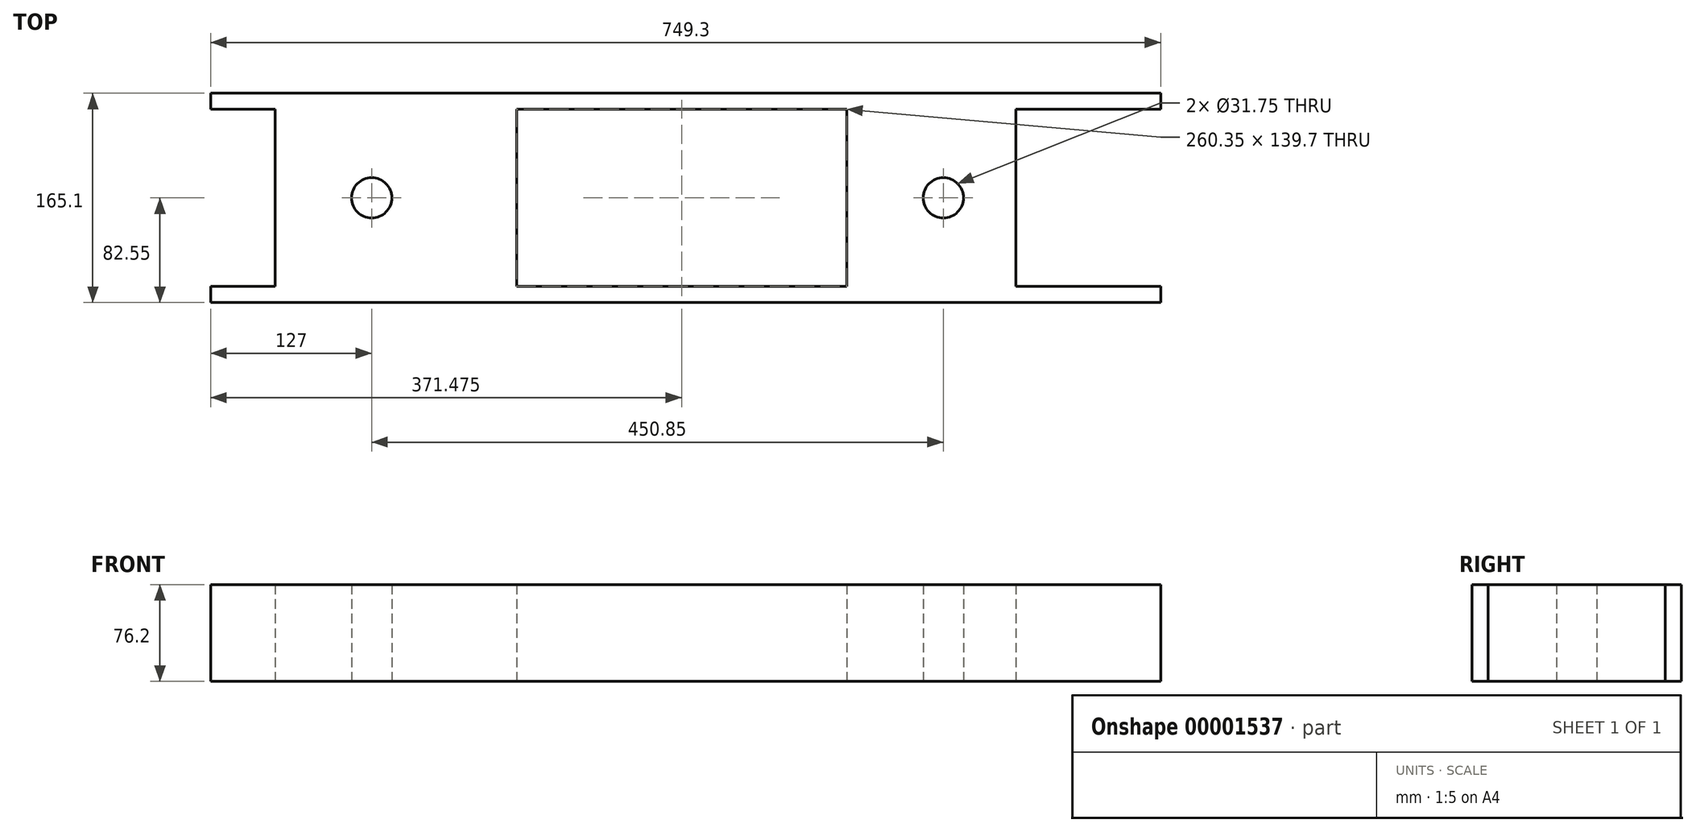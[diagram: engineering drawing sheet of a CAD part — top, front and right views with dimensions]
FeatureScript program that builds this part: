
annotation { "Feature Type Name" : "Feature", "Feature Type Description" : "" }
export const myFeature = defineFeature(function(context is Context, id is Id, definition is map)
    precondition{}
    {
        {
            var Q0;
            Q0=qCreatedBy(makeId("Top.planeOp"),FACE);
            var sketch = newSketch(context, id + "F0", { "sketchPlane" : qUnion([Q0])});
            skLineSegment(sketch, "E0.bottom", {"start": v(-374.65, 82.55) * mm, "end": v(374.65, 82.55) * mm});
            skLineSegment(sketch, "E0.top", {"start": v(-374.65, -82.55) * mm, "end": v(374.65, -82.55) * mm});
            skLineSegment(sketch, "E0.left", {"start": v(-374.65, 82.55) * mm, "end": v(-374.65, 69.85) * mm});
            skLineSegment(sketch, "E0.right", {"start": v(374.65, 82.55) * mm, "end": v(374.65, 69.85) * mm});
            skLineSegment(sketch, "E1", {"start": v(-247.65, 173.8) * mm, "end": v(-247.65, -177.5) * mm, "construction": true});
            skLineSegment(sketch, "E2", {"start": v(203.2, 146.7) * mm, "end": v(203.2, -191.95) * mm, "construction": true});
            skLineSegment(sketch, "E3.left", {"start": v(-323.85, 69.85) * mm, "end": v(-323.85, -69.85) * mm});
            skLineSegment(sketch, "E3.right", {"start": v(-133.35, 69.85) * mm, "end": v(-133.35, -69.85) * mm});
            skLineSegment(sketch, "E4.left", {"start": v(127, 69.85) * mm, "end": v(127, -69.85) * mm});
            skLineSegment(sketch, "E4.right", {"start": v(260.35, 69.85) * mm, "end": v(260.35, -69.85) * mm});
            skCircle(sketch, "E5", {"center": v(-247.65, 0) * mm, "radius": 15.88 * mm});
            skCircle(sketch, "E6", {"center": v(203.2, 0) * mm, "radius": 15.88 * mm});
            skLineSegment(sketch, "E7", {"start": v(-323.85, 69.85) * mm, "end": v(-374.65, 69.85) * mm});
            skLineSegment(sketch, "E8", {"start": v(-133.35, 69.85) * mm, "end": v(127, 69.85) * mm});
            skLineSegment(sketch, "E9", {"start": v(260.35, 69.85) * mm, "end": v(374.65, 69.85) * mm});
            skLineSegment(sketch, "E10", {"start": v(260.35, -69.85) * mm, "end": v(374.65, -69.85) * mm});
            skLineSegment(sketch, "E11", {"start": v(127, -69.85) * mm, "end": v(-133.35, -69.85) * mm});
            skLineSegment(sketch, "E12", {"start": v(-323.85, -69.85) * mm, "end": v(-374.65, -69.85) * mm});
            skLineSegment(sketch, "E13.trimOffspring", {"start": v(-374.65, -69.85) * mm, "end": v(-374.65, -82.55) * mm});
            skLineSegment(sketch, "E14.trimOffspring", {"start": v(374.65, -69.85) * mm, "end": v(374.65, -82.55) * mm});
            skSolve(sketch);
        }
        {
            var Q0;
            Q0=makeQuery(id+"F0.imprint","IMPRINT",FACE,{"disambiguationData":[TD([[makeQuery(id+"F0.imprint","IMPRINT",EDGE,{"derivedFrom":sQuery(id+"F0.wireOp",EDGE,"E0.bottom")}),-1.0]])]});
            extrude(context, id + "F1", {"entities" : qUnion([Q0]), "depth" : 76.2 * mm});
        }
    });
